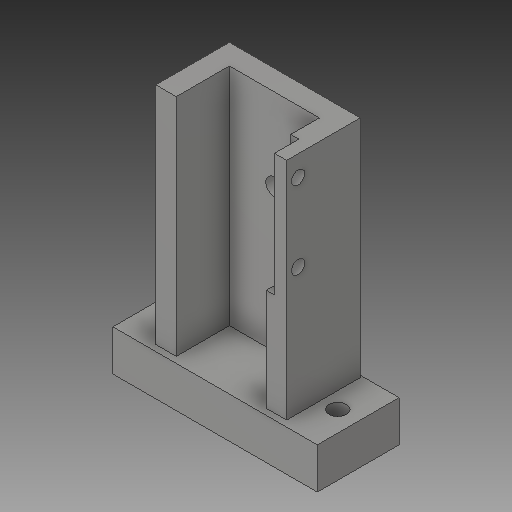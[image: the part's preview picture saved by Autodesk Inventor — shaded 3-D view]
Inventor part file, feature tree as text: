
AUTODESK INVENTOR PART (.ipt)
format: ipt  version: 2019 (Build 230136000, 136)  size: 319,488 bytes
history: native  units: mm
features: extrude x6, sketch x6, projected_geometry x1
ambient origin geometry x8: Origin, YZ Plane, XZ Plane, XY Plane, X Axis, Y Axis, Z Axis, Center Point
bodies: Body1 (feature_tree)
feature tree (13):
  extrude  "Extrusion3"  Depth=50.0mm
  extrude  "Extrusion4"  Depth=22.0mm
  extrude  "Extrusion5"  Depth=5.0mm
  extrude  "Extrusion6"  Depth=13.0mm
  extrude  "Extrusion7"  Depth=55.0mm
  extrude  "Extrusion8"  Depth=2.0mm
  sketch  "Sketch2"  dims[d10=20.0mm d11=50.0mm]
  sketch  "Sketch3"  dims[d12=10.0mm d13=0.0mm d14=22.0mm]
  projected_geometry  "Projected Loop1"
  sketch  "Sketch4"  dims[d15=5.0mm d16=5.0mm]
  sketch  "Sketch5"  dims[d17=0.5mm d18=13.0mm]
  sketch  "Sketch6"  dims[d19=55.0mm d20=0.0mm d21=4.25mm]
  sketch  "Sketch7"  dims[d23=13.0mm d24=0.0mm d26=4.25mm d27=10.0mm d28=5.0mm d29=10.0mm d30=0.0mm d32=34.875mm d33=3.25mm d34=3.25mm d35=19.0mm d36=31.0mm d37=2.8mm d38=10.0mm d39=0.0mm d40=6.0mm d41=30.0mm d42=2.0mm d43=0.0mm]
